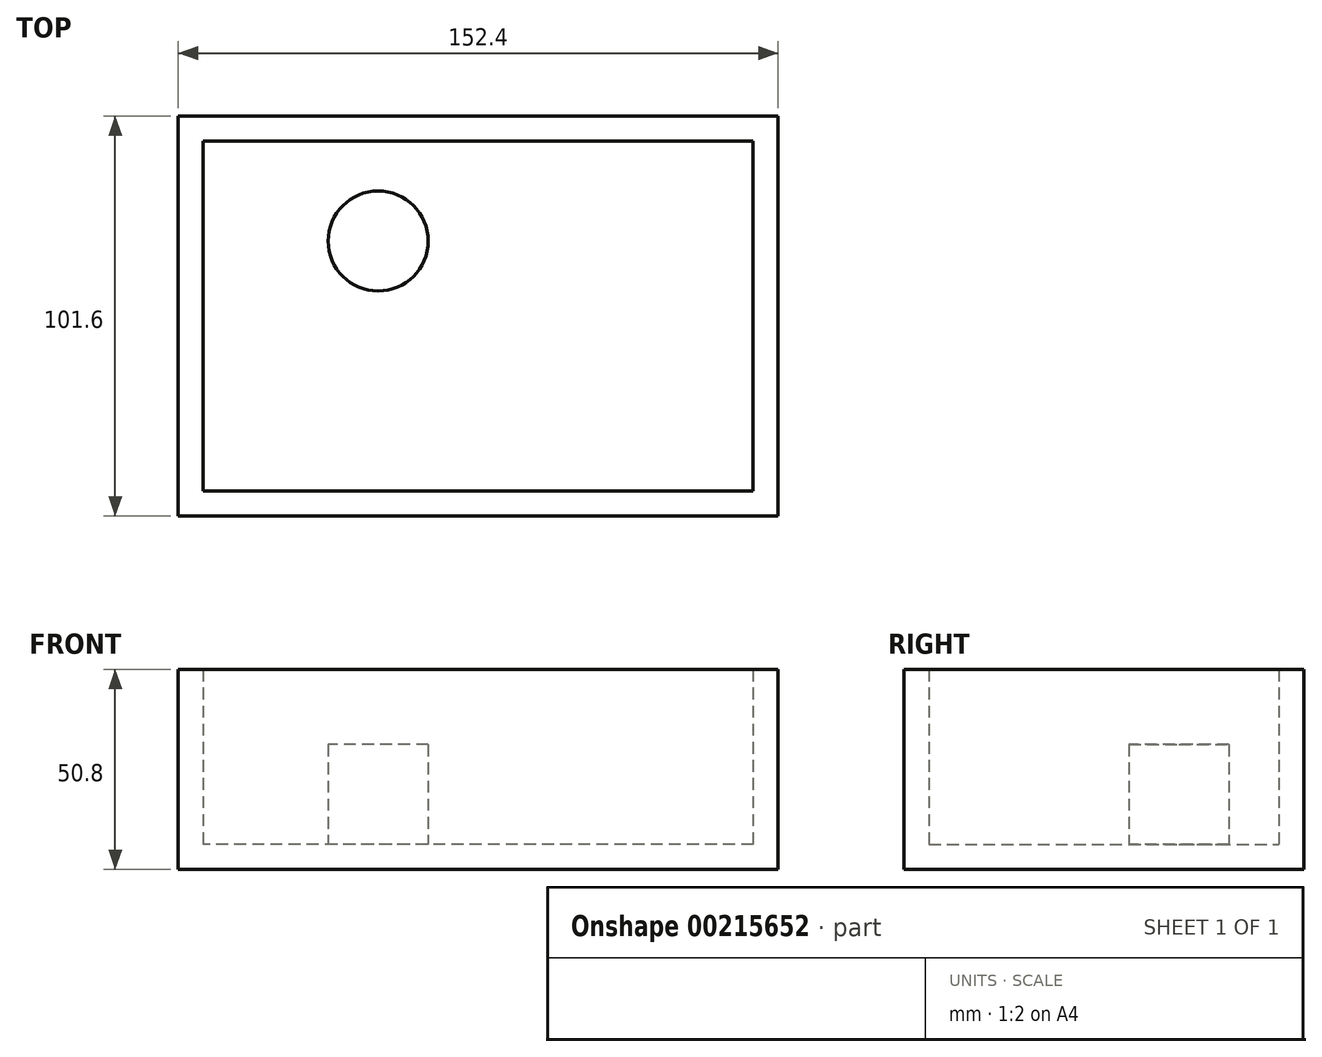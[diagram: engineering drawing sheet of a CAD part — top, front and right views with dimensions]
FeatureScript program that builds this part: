
annotation { "Feature Type Name" : "Feature", "Feature Type Description" : "" }
export const myFeature = defineFeature(function(context is Context, id is Id, definition is map)
    precondition{}
    {
        {
            var Q0;
            Q0=qCreatedBy(makeId("Top.planeOp"),FACE);
            var sketch = newSketch(context, id + "F0", { "sketchPlane" : qUnion([Q0])});
            skLineSegment(sketch, "E0.bottom", {"start": v(76.2, -50.8) * mm, "end": v(-76.2, -50.8) * mm});
            skLineSegment(sketch, "E0.top", {"start": v(76.2, 50.8) * mm, "end": v(-76.2, 50.8) * mm});
            skLineSegment(sketch, "E0.left", {"start": v(76.2, -50.8) * mm, "end": v(76.2, 50.8) * mm});
            skLineSegment(sketch, "E0.right", {"start": v(-76.2, -50.8) * mm, "end": v(-76.2, 50.8) * mm});
            skPoint(sketch, "E0.middle", {"position": v(0, 0) * mm});
            skSolve(sketch);
        }
        {
            var Q0;
            Q0 = qSketchRegion(id + "F0", true);
            extrude(context, id + "F1", {"entities" : qUnion([Q0]), "depth" : 50.8 * mm});
        }
        {
            var Q0;
            Q0=makeQuery(id+"F1.opExtrude","CAP_FACE",FACE,{"disambiguationData":[OSD([sQuery(id+"F0.wireOp",EDGE,"E0.bottom"),sQuery(id+"F0.wireOp",EDGE,"E0.top"),sQuery(id+"F0.wireOp",EDGE,"E0.left"),sQuery(id+"F0.wireOp",EDGE,"E0.right")])],"isStart":false});
            shell(context, id + "F2", {"entities" : qUnion([Q0]), "thickness" : 6.35 * mm});
        }
        {
            var Q0;
            Q0=makeQuery(id+"F2.opShell","OFFSET_FACE",FACE,{"disambiguationData":[OSD([sQuery(id+"F0.wireOp",EDGE,"E0.bottom"),sQuery(id+"F0.wireOp",EDGE,"E0.top"),sQuery(id+"F0.wireOp",EDGE,"E0.left"),sQuery(id+"F0.wireOp",EDGE,"E0.right")])]});
            var sketch = newSketch(context, id + "F3", { "sketchPlane" : qUnion([Q0])});
            skCircle(sketch, "E1", {"center": v(-25.4, 19.05) * mm, "radius": 12.7 * mm});
            skSolve(sketch);
        }
        {
            var Q0;
            Q0 = qSketchRegion(id + "F3", true);
            extrude(context, id + "F4", {"entities" : qUnion([Q0]), "operationType" : NewBodyOperationType.ADD, "depth" : 25.4 * mm});
        }
    });
